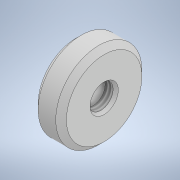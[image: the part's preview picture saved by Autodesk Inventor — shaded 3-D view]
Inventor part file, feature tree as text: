
AUTODESK INVENTOR PART (.ipt)
format: ipt  version: 2022 (Build 260153000, 153)  size: 124,416 bytes
history: native  units: mm
features: sketch x2, other x1, hole x1, thread x1, projected_geometry x1, revolve x1
ambient origin geometry x8: Origin, YZ Plane, XZ Plane, XY Plane, X Axis, Y Axis, Z Axis, Center Point
bodies: Body1 (feature_tree)
feature tree (7):
  other  "Твердое тело1"
  hole  "Отверстие1"  [1 undecoded]
  thread  "Резьба1"
  sketch  "Эскиз2"
  projected_geometry  "Спроецированная петля1"
  sketch  "Эскиз1"
  revolve  "Вращение1"
note: 1 required parameter value undecoded (feature->parameter linkage not recoverable at this tier; creation-order binding heuristic only, values carry confidence <= 0.55)
